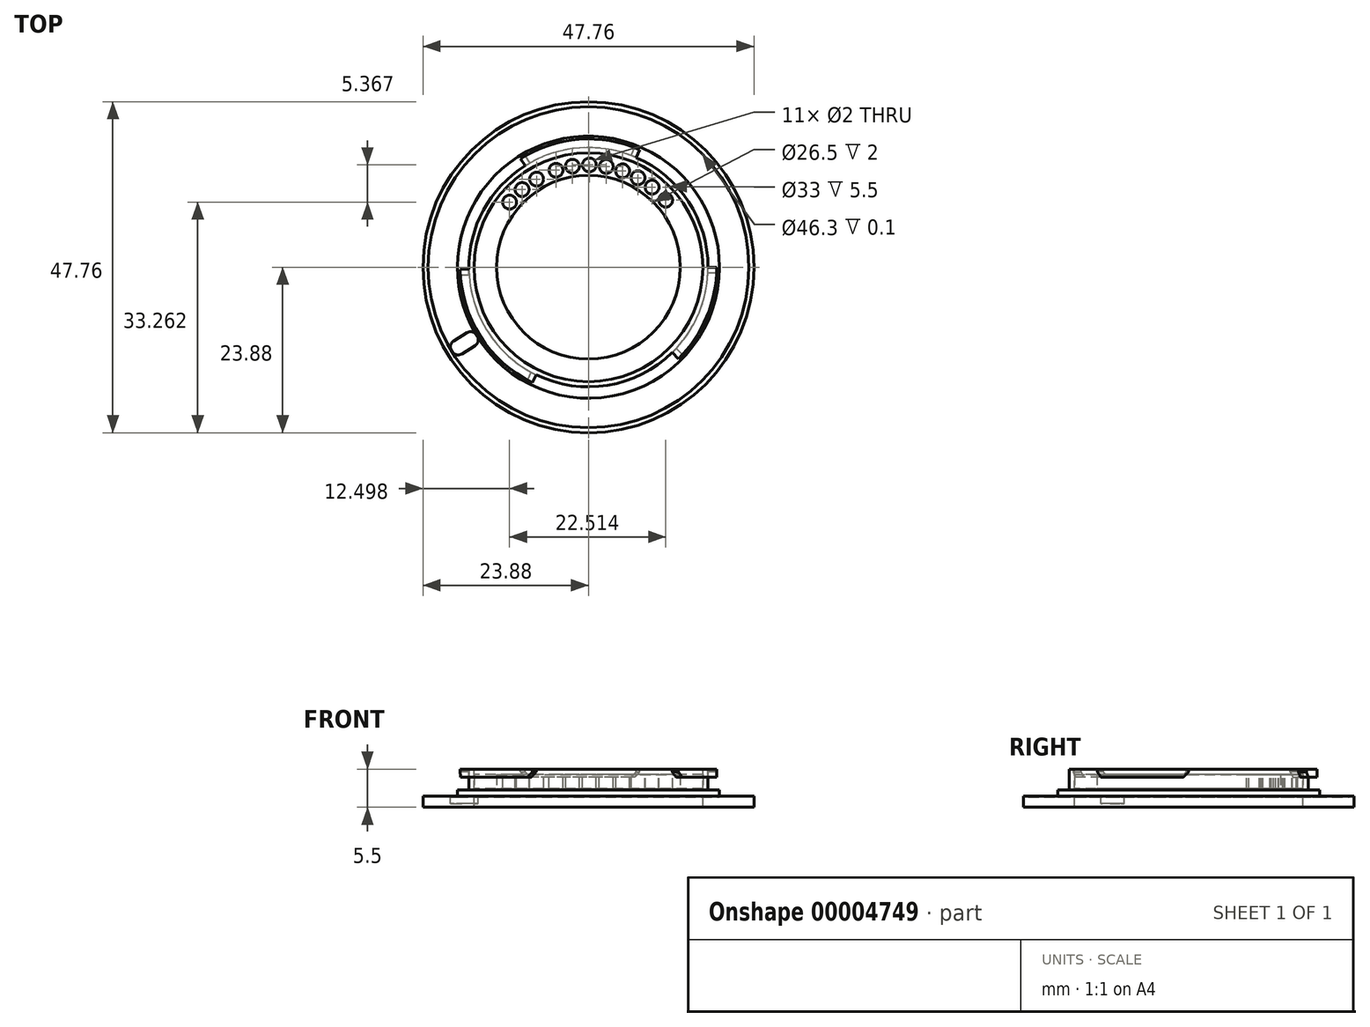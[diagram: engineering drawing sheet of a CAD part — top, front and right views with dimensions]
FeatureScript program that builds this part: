
annotation { "Feature Type Name" : "Feature", "Feature Type Description" : "" }
export const myFeature = defineFeature(function(context is Context, id is Id, definition is map)
    precondition{}
    {
        {
            var Q0;
            Q0=qCreatedBy(makeId("Top.planeOp"),FACE);
            var sketch = newSketch(context, id + "F0", { "sketchPlane" : qUnion([Q0])});
            skCircle(sketch, "E0", {"center": v(0, 0) * mm, "radius": 23.88 * mm});
            skCircle(sketch, "E1", {"center": v(0, 0) * mm, "radius": 23.15 * mm, "construction": true});
            skCircle(sketch, "E2", {"center": v(0, 0) * mm, "radius": 18.9 * mm, "construction": true});
            skCircle(sketch, "E3", {"center": v(0, 0) * mm, "radius": 16.5 * mm});
            skArc(sketch, "E4", {"start": v(-9.14, 14.63) * mm, "mid": v(-15.16, 8.23) * mm, "end": v(-17.25, -0.3) * mm, "construction": true});
            skArc(sketch, "E5", {"start": v(-18.5, -0.32) * mm, "mid": v(-15.6, -9.94) * mm, "end": v(-8.1, -16.63) * mm, "construction": true});
            skLineSegment(sketch, "E6", {"start": v(-19.74, -12.1) * mm, "end": v(0, 0) * mm, "construction": true});
            skLineSegment(sketch, "E7", {"start": v(-9.8, 15.69) * mm, "end": v(0, 0) * mm, "construction": true});
            skLineSegment(sketch, "E8", {"start": v(7.38, 16.97) * mm, "end": v(0, 0) * mm, "construction": true});
            skLineSegment(sketch, "E9", {"start": v(18.5, 0) * mm, "end": v(0, 0) * mm, "construction": true});
            skLineSegment(sketch, "E10", {"start": v(12.97, -13.2) * mm, "end": v(0, 0) * mm, "construction": true});
            skLineSegment(sketch, "E11", {"start": v(-8.1, -16.63) * mm, "end": v(0, 0) * mm, "construction": true});
            skLineSegment(sketch, "E12", {"start": v(-18.5, -0.32) * mm, "end": v(0, 0) * mm, "construction": true});
            skCircle(sketch, "E13", {"center": v(0, 0) * mm, "radius": 13.25 * mm, "construction": true});
            skLineSegment(sketch, "E14", {"start": v(-16.14, -9.77) * mm, "end": v(-16.04, -9.94) * mm});
            skLineSegment(sketch, "E15", {"start": v(-16.37, -11.32) * mm, "end": v(-18.29, -12.5) * mm, "construction": true});
            skLineSegment(sketch, "E16", {"start": v(-17.51, -9.44) * mm, "end": v(-19.44, -10.62) * mm, "construction": true});
            skLineSegment(sketch, "E17", {"start": v(-19.77, -12) * mm, "end": v(-19.66, -12.17) * mm});
            skLineSegment(sketch, "E18", {"start": v(-9.8, 15.69) * mm, "end": v(-9.14, 14.63) * mm});
            skLineSegment(sketch, "E19", {"start": v(7.38, 16.97) * mm, "end": v(6.88, 15.82) * mm});
            skLineSegment(sketch, "E20", {"start": v(17.25, 0) * mm, "end": v(18.5, 0) * mm});
            skLineSegment(sketch, "E21", {"start": v(12.1, -12.3) * mm, "end": v(12.97, -13.2) * mm});
            skLineSegment(sketch, "E22", {"start": v(-7.56, -15.5) * mm, "end": v(-8.1, -16.63) * mm});
            skLineSegment(sketch, "E23", {"start": v(-17.25, -0.3) * mm, "end": v(-18.5, -0.32) * mm});
            skArc(sketch, "E24.trimOffspring", {"start": v(17.25, 0) * mm, "mid": v(14.43, 9.46) * mm, "end": v(6.88, 15.82) * mm, "construction": true});
            skArc(sketch, "E25.trimOffspring", {"start": v(-7.56, -15.5) * mm, "mid": v(2.77, -17.03) * mm, "end": v(12.1, -12.3) * mm, "construction": true});
            skArc(sketch, "E26.trimOffspring", {"start": v(7.38, 16.97) * mm, "mid": v(-1.37, 18.45) * mm, "end": v(-9.8, 15.69) * mm, "construction": true});
            skArc(sketch, "E27.trimOffspring", {"start": v(12.97, -13.2) * mm, "mid": v(17.06, -7.15) * mm, "end": v(18.5, 0) * mm, "construction": true});
            skCircle(sketch, "E28", {"center": v(-11.38, 9.38) * mm, "radius": 1 * mm});
            skLineSegment(sketch, "E29", {"start": v(-11.38, 9.38) * mm, "end": v(0, 0) * mm, "construction": true});
            skCircle(sketch, "E30", {"center": v(-7.49, 12.7) * mm, "radius": 1 * mm});
            skLineSegment(sketch, "E31", {"start": v(-7.49, 12.7) * mm, "end": v(0, 0) * mm, "construction": true});
            skLineSegment(sketch, "E32", {"start": v(0, 0) * mm, "end": v(11.13, 9.68) * mm, "construction": true});
            skCircle(sketch, "E33", {"center": v(11.13, 9.68) * mm, "radius": 1 * mm});
            skLineSegment(sketch, "E34", {"start": v(9.18, 11.54) * mm, "end": v(0, 0) * mm, "construction": true});
            skLineSegment(sketch, "E35", {"start": v(7.15, 12.9) * mm, "end": v(0, 0) * mm, "construction": true});
            skLineSegment(sketch, "E36", {"start": v(4.92, 13.9) * mm, "end": v(0, 0) * mm, "construction": true});
            skLineSegment(sketch, "E37", {"start": v(2.56, 14.53) * mm, "end": v(0, 0) * mm, "construction": true});
            skLineSegment(sketch, "E38", {"start": v(0.13, 14.75) * mm, "end": v(0, 0) * mm, "construction": true});
            skLineSegment(sketch, "E39", {"start": v(-2.3, 14.57) * mm, "end": v(0, 0) * mm, "construction": true});
            skLineSegment(sketch, "E40", {"start": v(-4.68, 13.99) * mm, "end": v(0, 0) * mm, "construction": true});
            skLineSegment(sketch, "E41", {"start": v(-9.58, 11.22) * mm, "end": v(0, 0) * mm, "construction": true});
            skCircle(sketch, "E42", {"center": v(-9.58, 11.22) * mm, "radius": 1 * mm});
            skCircle(sketch, "E43", {"center": v(-4.68, 13.99) * mm, "radius": 1 * mm});
            skCircle(sketch, "E44", {"center": v(-2.3, 14.57) * mm, "radius": 1 * mm});
            skCircle(sketch, "E45", {"center": v(0.13, 14.75) * mm, "radius": 1 * mm});
            skCircle(sketch, "E46", {"center": v(2.56, 14.53) * mm, "radius": 1 * mm});
            skCircle(sketch, "E47", {"center": v(4.92, 13.9) * mm, "radius": 1 * mm});
            skCircle(sketch, "E48", {"center": v(7.15, 12.9) * mm, "radius": 1 * mm});
            skCircle(sketch, "E49", {"center": v(9.18, 11.54) * mm, "radius": 1 * mm});
            skPoint(sketch, "E50.visualSharp", {"position": v(-20.3, -11.14) * mm});
            skArc(sketch, "E50.filletArc", {"start": v(-19.44, -10.62) * mm, "mid": v(-19.89, -11.24) * mm, "end": v(-19.77, -12) * mm, "construction": true});
            skPoint(sketch, "E51.visualSharp", {"position": v(-19.14, -13.02) * mm});
            skLineSegment(sketch, "E52", {"start": v(-19.66, -12.17) * mm, "end": v(-19.66, -12.17) * mm});
            skArc(sketch, "E53.filletArc", {"start": v(-19.66, -12.17) * mm, "mid": v(-19.04, -12.62) * mm, "end": v(-18.29, -12.5) * mm, "construction": true});
            skPoint(sketch, "E54.visualSharp", {"position": v(-16.66, -8.92) * mm});
            skArc(sketch, "E54.filletArc", {"start": v(-16.14, -9.77) * mm, "mid": v(-16.76, -9.32) * mm, "end": v(-17.51, -9.44) * mm, "construction": true});
            skPoint(sketch, "E55.visualSharp", {"position": v(-15.51, -10.8) * mm});
            skArc(sketch, "E55.filletArc", {"start": v(-16.37, -11.32) * mm, "mid": v(-15.92, -10.7) * mm, "end": v(-16.04, -9.94) * mm, "construction": true});
            skSolve(sketch);
        }
        {
            var Q0;
            Q0=makeQuery(id+"F0.imprint","IMPRINT",FACE,{"disambiguationData":[TD([[makeQuery(id+"F0.imprint","IMPRINT",EDGE,{"derivedFrom":sQuery(id+"F0.wireOp",EDGE,"E0")}),1.0]])]});
            extrude(context, id + "F1", {"entities" : qUnion([Q0]), "oppositeDirection" : true, "depth" : 1.5 * mm});
        }
        {
            var Q0;
            Q0=makeQuery(id+"F0.imprint","IMPRINT",FACE,{"disambiguationData":[TD([[makeQuery(id+"F0.imprint","IMPRINT",EDGE,{"derivedFrom":sQuery(id+"F0.wireOp",EDGE,"E0")}),1.0]])]});
            var sketch = newSketch(context, id + "F2", { "sketchPlane" : qUnion([Q0])});
            skCircle(sketch, "E56.0", {"center": v(0, 0) * mm, "radius": 23.88 * mm});
            skCircle(sketch, "E57.0", {"center": v(0, 0) * mm, "radius": 23.15 * mm});
            skSolve(sketch);
        }
        {
            var Q0;
            Q0=makeQuery(id+"F2.imprint","IMPRINT",FACE,{"disambiguationData":[TD([[makeQuery(id+"F2.imprint","IMPRINT",EDGE,{"derivedFrom":sQuery(id+"F2.wireOp",EDGE,"E56.0")}),1.0]])]});
            extrude(context, id + "F3", {"entities" : qUnion([Q0]), "operationType" : NewBodyOperationType.ADD, "depth" : 0.1 * mm});
        }
        {
            var Q0;
            Q0=makeQuery(id+"F0.imprint","IMPRINT",FACE,{"disambiguationData":[TD([[makeQuery(id+"F0.imprint","IMPRINT",EDGE,{"derivedFrom":sQuery(id+"F0.wireOp",EDGE,"E0")}),1.0]])]});
            var sketch = newSketch(context, id + "F4", { "sketchPlane" : qUnion([Q0])});
            skCircle(sketch, "E58.0", {"center": v(0, 0) * mm, "radius": 18.9 * mm});
            skCircle(sketch, "E59.0", {"center": v(0, 0) * mm, "radius": 16.5 * mm});
            skSolve(sketch);
        }
        {
            var Q0;
            Q0=makeQuery(id+"F4.imprint","IMPRINT",FACE,{"disambiguationData":[TD([[makeQuery(id+"F4.imprint","IMPRINT",EDGE,{"derivedFrom":sQuery(id+"F4.wireOp",EDGE,"E58.0")}),1.0]])]});
            extrude(context, id + "F5", {"entities" : qUnion([Q0]), "operationType" : NewBodyOperationType.ADD, "depth" : 1 * mm});
        }
        {
            var Q0;
            Q0=makeQuery(id+"F5.opExtrude","CAP_FACE",FACE,{"disambiguationData":[OSD([sQuery(id+"F4.wireOp",EDGE,"E58.0"),sQuery(id+"F4.wireOp",EDGE,"E59.0")])],"isStart":false});
            var sketch = newSketch(context, id + "F6", { "sketchPlane" : qUnion([Q0])});
            skCircle(sketch, "E60.0", {"center": v(0, 0) * mm, "radius": 16.5 * mm});
            skCircle(sketch, "E61.converted", {"center": v(0, 0) * mm, "radius": 17.25 * mm});
            skPoint(sketch, "E62.orphan", {"position": v(-17.25, -0.3) * mm});
            skSolve(sketch);
        }
        {
            var Q0;
            Q0=makeQuery(id+"F6.imprint","IMPRINT",FACE,{"disambiguationData":[TD([[makeQuery(id+"F6.imprint","IMPRINT",EDGE,{"derivedFrom":sQuery(id+"F6.wireOp",EDGE,"E60.0")}),-1.0]])]});
            extrude(context, id + "F7", {"entities" : qUnion([Q0]), "operationType" : NewBodyOperationType.ADD, "depth" : 3 * mm});
        }
        {
            var Q0;
            Q0=makeQuery(id+"F7.opExtrude","CAP_FACE",FACE,{"disambiguationData":[OSD([sQuery(id+"F6.wireOp",EDGE,"E60.0"),sQuery(id+"F6.wireOp",EDGE,"E61.converted")])],"isStart":false});
            var sketch = newSketch(context, id + "F8", { "sketchPlane" : qUnion([Q0])});
            skCircle(sketch, "E63.0", {"center": v(0, 0) * mm, "radius": 16.5 * mm});
            skLineSegment(sketch, "E64.0", {"start": v(-17.25, -0.3) * mm, "end": v(-18.5, -0.32) * mm});
            skArc(sketch, "E65.0", {"start": v(-18.5, -0.32) * mm, "mid": v(-15.6, -9.94) * mm, "end": v(-8.1, -16.63) * mm});
            skLineSegment(sketch, "E66.0", {"start": v(-7.56, -15.5) * mm, "end": v(-8.1, -16.63) * mm});
            skArc(sketch, "E67.0", {"start": v(-7.56, -15.5) * mm, "mid": v(2.77, -17.03) * mm, "end": v(12.1, -12.3) * mm});
            skLineSegment(sketch, "E68.0", {"start": v(12.1, -12.3) * mm, "end": v(12.97, -13.2) * mm});
            skArc(sketch, "E69.0", {"start": v(12.97, -13.2) * mm, "mid": v(17.06, -7.15) * mm, "end": v(18.5, 0) * mm});
            skLineSegment(sketch, "E70.0", {"start": v(17.25, 0) * mm, "end": v(18.5, 0) * mm});
            skArc(sketch, "E71.0", {"start": v(17.25, 0) * mm, "mid": v(14.43, 9.46) * mm, "end": v(6.88, 15.82) * mm});
            skLineSegment(sketch, "E72.0", {"start": v(7.38, 16.97) * mm, "end": v(6.88, 15.82) * mm});
            skArc(sketch, "E73.0", {"start": v(7.38, 16.97) * mm, "mid": v(-1.37, 18.45) * mm, "end": v(-9.8, 15.69) * mm});
            skLineSegment(sketch, "E74.0", {"start": v(-9.8, 15.69) * mm, "end": v(-9.14, 14.63) * mm});
            skArc(sketch, "E75.0", {"start": v(-9.14, 14.63) * mm, "mid": v(-15.16, 8.23) * mm, "end": v(-17.25, -0.3) * mm});
            skSolve(sketch);
        }
        {
            var Q0;
            {var subQ3=sQuery(id+"F8.wireOp",EDGE,"E64.0");var subQ8=sQuery(id+"F8.wireOp",EDGE,"E68.0");var subQ11=sQuery(id+"F8.wireOp",EDGE,"E72.0");Q0=qUnion([makeQuery(id+"F8.imprint","IMPRINT",FACE,{"disambiguationData":[TD([[makeQuery(id+"F8.imprint","IMPRINT",EDGE,{"derivedFrom":subQ3}),1.0]])]}),makeQuery(id+"F8.imprint","IMPRINT",FACE,{"disambiguationData":[TD([[makeQuery(id+"F8.imprint","IMPRINT",EDGE,{"derivedFrom":subQ8}),1.0]])]}),makeQuery(id+"F8.imprint","IMPRINT",FACE,{"disambiguationData":[TD([[makeQuery(id+"F8.imprint","IMPRINT",EDGE,{"derivedFrom":subQ11}),-1.0]])]}),makeQuery(id+"F8.imprint","IMPRINT",FACE,{"disambiguationData":[TD([[makeQuery(id+"F8.imprint","IMPRINT",EDGE,{"derivedFrom":sQuery(id+"F8.wireOp",EDGE,"E63.0")}),-1.0]])]})]);}
            extrude(context, id + "F9", {"entities" : qUnion([Q0]), "operationType" : NewBodyOperationType.ADD, "oppositeDirection" : true, "depth" : 1.2 * mm});
        }
        {
            var Q0;
            Q0=makeQuery(id+"F1.opExtrude","CAP_FACE",FACE,{"disambiguationData":[OSD([sQuery(id+"F0.wireOp",EDGE,"E0"),sQuery(id+"F0.wireOp",EDGE,"E3")])],"isStart":true});
            var sketch = newSketch(context, id + "F10", { "sketchPlane" : qUnion([Q0])});
            skArc(sketch, "E76.0", {"start": v(-19.66, -12.17) * mm, "mid": v(-19.04, -12.62) * mm, "end": v(-18.29, -12.5) * mm});
            skLineSegment(sketch, "E77.0", {"start": v(-16.37, -11.32) * mm, "end": v(-18.29, -12.5) * mm});
            skArc(sketch, "E78.0", {"start": v(-16.37, -11.32) * mm, "mid": v(-15.92, -10.7) * mm, "end": v(-16.04, -9.94) * mm});
            skArc(sketch, "E79.0", {"start": v(-19.44, -10.62) * mm, "mid": v(-19.89, -11.24) * mm, "end": v(-19.77, -12) * mm});
            skLineSegment(sketch, "E80.0", {"start": v(-17.51, -9.44) * mm, "end": v(-19.44, -10.62) * mm});
            skArc(sketch, "E81.0", {"start": v(-16.14, -9.77) * mm, "mid": v(-16.76, -9.32) * mm, "end": v(-17.51, -9.44) * mm});
            skLineSegment(sketch, "E82.0", {"start": v(-16.14, -9.77) * mm, "end": v(-16.04, -9.94) * mm});
            skLineSegment(sketch, "E83.0", {"start": v(-19.77, -12) * mm, "end": v(-19.66, -12.17) * mm});
            skSolve(sketch);
        }
        {
            var Q0;
            {var subQ8=sQuery(id+"F10.wireOp",EDGE,"E82.0");Q0=qUnion([makeQuery(id+"F10.imprint","IMPRINT",FACE,{"disambiguationData":[TD([[makeQuery(id+"F10.imprint","IMPRINT",EDGE,{"derivedFrom":sQuery(id+"F10.wireOp",EDGE,"E76.0")}),1.0]])]}),makeQuery(id+"F10.imprint","IMPRINT",FACE,{"disambiguationData":[TD([[makeQuery(id+"F10.imprint","IMPRINT",EDGE,{"derivedFrom":subQ8}),-1.0]])]})]);}
            extrude(context, id + "F11", {"entities" : qUnion([Q0]), "operationType" : NewBodyOperationType.REMOVE, "oppositeDirection" : true, "depth" : 1 * mm});
        }
        {
            var Q0;
            Q0=makeQuery(id+"F9.opExtrude","CAP_EDGE",EDGE,{"disambiguationData":[OSD([sQuery(id+"F8.wireOp",EDGE,"E72.0")])],"isStart":false});
            var Q1;
            Q1=makeQuery(id+"F9.opExtrude","CAP_EDGE",EDGE,{"disambiguationData":[OSD([sQuery(id+"F8.wireOp",EDGE,"E74.0")])],"isStart":false});
            var Q2;
            Q2=makeQuery(id+"F9.opExtrude","CAP_EDGE",EDGE,{"disambiguationData":[OSD([sQuery(id+"F8.wireOp",EDGE,"E70.0")])],"isStart":false});
            var Q3;
            Q3=makeQuery(id+"F9.opExtrude","CAP_EDGE",EDGE,{"disambiguationData":[OSD([sQuery(id+"F8.wireOp",EDGE,"E68.0")])],"isStart":false});
            var Q4;
            Q4=makeQuery(id+"F9.opExtrude","CAP_EDGE",EDGE,{"disambiguationData":[OSD([sQuery(id+"F8.wireOp",EDGE,"E66.0")])],"isStart":false});
            var Q5;
            Q5=makeQuery(id+"F9.opExtrude","CAP_EDGE",EDGE,{"disambiguationData":[OSD([sQuery(id+"F8.wireOp",EDGE,"E64.0")])],"isStart":false});
            chamfer(context, id + "F12", {"entities" : qUnion([Q0, Q1, Q2, Q3, Q4, Q5]), "width" : 0.8 * mm, "tangentPropagation" : true});
        }
        {
            var Q0;
            Q0=makeQuery(id+"F1.opExtrude","CAP_FACE",FACE,{"disambiguationData":[OSD([sQuery(id+"F0.wireOp",EDGE,"E0"),sQuery(id+"F0.wireOp",EDGE,"E3")])],"isStart":false});
            var sketch = newSketch(context, id + "F13", { "sketchPlane" : qUnion([Q0])});
            skCircle(sketch, "E84.0", {"center": v(0, 0) * mm, "radius": 16.5 * mm});
            skCircle(sketch, "E85.0", {"center": v(0, 0) * mm, "radius": 13.25 * mm});
            skSolve(sketch);
        }
        {
            var Q0;
            Q0=makeQuery(id+"F13.imprint","IMPRINT",FACE,{"disambiguationData":[TD([[makeQuery(id+"F13.imprint","IMPRINT",EDGE,{"derivedFrom":sQuery(id+"F13.wireOp",EDGE,"E84.0")}),-1.0]])]});
            extrude(context, id + "F14", {"entities" : qUnion([Q0]), "oppositeDirection" : true, "depth" : 2 * mm});
        }
        {
            var Q0;
            Q0=makeQuery(id+"F14.opExtrude","SWEPT_BODY",BODY,{"disambiguationData":[OSD([sQuery(id+"F13.wireOp",EDGE,"E84.0"),sQuery(id+"F13.wireOp",EDGE,"E85.0")])]});
            var Q1;
            Q1=makeQuery(id+"F9.boolean.opBoolean","MERGE",FACE,{"derivedFrom":[makeQuery(id+"F7.opExtrude","CAP_FACE",FACE,{"disambiguationData":[OSD([sQuery(id+"F6.wireOp",EDGE,"E60.0"),sQuery(id+"F6.wireOp",EDGE,"E61.converted")])],"isStart":false}),makeQuery(id+"F9.opExtrude","CAP_FACE",FACE,{"disambiguationData":[OSD([sQuery(id+"F8.wireOp",EDGE,"E63.0"),sQuery(id+"F8.wireOp",EDGE,"E64.0"),sQuery(id+"F8.wireOp",EDGE,"E65.0"),sQuery(id+"F8.wireOp",EDGE,"E66.0"),sQuery(id+"F8.wireOp",EDGE,"E67.0"),sQuery(id+"F8.wireOp",EDGE,"E68.0"),sQuery(id+"F8.wireOp",EDGE,"E69.0"),sQuery(id+"F8.wireOp",EDGE,"E70.0"),sQuery(id+"F8.wireOp",EDGE,"E71.0"),sQuery(id+"F8.wireOp",EDGE,"E72.0"),sQuery(id+"F8.wireOp",EDGE,"E73.0"),sQuery(id+"F8.wireOp",EDGE,"E74.0"),sQuery(id+"F8.wireOp",EDGE,"E75.0")])],"isStart":true})]});
            transform(context, id + "F15", {"entities" : qUnion([Q0]), "transformType" : TransformType.TRANSLATION_DISTANCE, "transformDirection" : qUnion([Q1]), "distance" : 2.7 * mm, "makeCopy" : false});
        }
        {
            var Q0;
            Q0=makeQuery(id+"F14.opExtrude","CAP_FACE",FACE,{"disambiguationData":[OSD([sQuery(id+"F13.wireOp",EDGE,"E84.0"),sQuery(id+"F13.wireOp",EDGE,"E85.0")])],"isStart":false});
            var sketch = newSketch(context, id + "F16", { "sketchPlane" : qUnion([Q0])});
            skCircle(sketch, "E86.0", {"center": v(-11.38, 9.38) * mm, "radius": 1 * mm});
            skCircle(sketch, "E87.0", {"center": v(-9.58, 11.22) * mm, "radius": 1 * mm});
            skCircle(sketch, "E88.0", {"center": v(-7.49, 12.7) * mm, "radius": 1 * mm});
            skCircle(sketch, "E89.0", {"center": v(-4.68, 13.99) * mm, "radius": 1 * mm});
            skCircle(sketch, "E90.0", {"center": v(-2.3, 14.57) * mm, "radius": 1 * mm});
            skCircle(sketch, "E91.0", {"center": v(0.13, 14.75) * mm, "radius": 1 * mm});
            skCircle(sketch, "E92.0", {"center": v(2.56, 14.53) * mm, "radius": 1 * mm});
            skCircle(sketch, "E93.0", {"center": v(4.92, 13.9) * mm, "radius": 1 * mm});
            skCircle(sketch, "E94.0", {"center": v(7.15, 12.9) * mm, "radius": 1 * mm});
            skCircle(sketch, "E95.0", {"center": v(9.18, 11.54) * mm, "radius": 1 * mm});
            skCircle(sketch, "E96.0", {"center": v(11.13, 9.68) * mm, "radius": 1 * mm});
            skSolve(sketch);
        }
        {
            var Q0;
            Q0=makeQuery(id+"F16.imprint","IMPRINT",FACE,{"disambiguationData":[TD([[makeQuery(id+"F16.imprint","IMPRINT",EDGE,{"derivedFrom":sQuery(id+"F16.wireOp",EDGE,"E86.0")}),1.0]])]});
            var Q1;
            Q1=makeQuery(id+"F16.imprint","IMPRINT",FACE,{"disambiguationData":[TD([[makeQuery(id+"F16.imprint","IMPRINT",EDGE,{"derivedFrom":sQuery(id+"F16.wireOp",EDGE,"E87.0")}),1.0]])]});
            var Q2;
            Q2=makeQuery(id+"F16.imprint","IMPRINT",FACE,{"disambiguationData":[TD([[makeQuery(id+"F16.imprint","IMPRINT",EDGE,{"derivedFrom":sQuery(id+"F16.wireOp",EDGE,"E88.0")}),1.0]])]});
            var Q3;
            Q3=makeQuery(id+"F16.imprint","IMPRINT",FACE,{"disambiguationData":[TD([[makeQuery(id+"F16.imprint","IMPRINT",EDGE,{"derivedFrom":sQuery(id+"F16.wireOp",EDGE,"E89.0")}),1.0]])]});
            var Q4;
            Q4=makeQuery(id+"F16.imprint","IMPRINT",FACE,{"disambiguationData":[TD([[makeQuery(id+"F16.imprint","IMPRINT",EDGE,{"derivedFrom":sQuery(id+"F16.wireOp",EDGE,"E90.0")}),1.0]])]});
            var Q5;
            Q5=makeQuery(id+"F16.imprint","IMPRINT",FACE,{"disambiguationData":[TD([[makeQuery(id+"F16.imprint","IMPRINT",EDGE,{"derivedFrom":sQuery(id+"F16.wireOp",EDGE,"E91.0")}),1.0]])]});
            var Q6;
            Q6=makeQuery(id+"F16.imprint","IMPRINT",FACE,{"disambiguationData":[TD([[makeQuery(id+"F16.imprint","IMPRINT",EDGE,{"derivedFrom":sQuery(id+"F16.wireOp",EDGE,"E92.0")}),1.0]])]});
            var Q7;
            Q7=makeQuery(id+"F16.imprint","IMPRINT",FACE,{"disambiguationData":[TD([[makeQuery(id+"F16.imprint","IMPRINT",EDGE,{"derivedFrom":sQuery(id+"F16.wireOp",EDGE,"E93.0")}),1.0]])]});
            var Q8;
            Q8=makeQuery(id+"F16.imprint","IMPRINT",FACE,{"disambiguationData":[TD([[makeQuery(id+"F16.imprint","IMPRINT",EDGE,{"derivedFrom":sQuery(id+"F16.wireOp",EDGE,"E94.0")}),1.0]])]});
            var Q9;
            Q9=makeQuery(id+"F16.imprint","IMPRINT",FACE,{"disambiguationData":[TD([[makeQuery(id+"F16.imprint","IMPRINT",EDGE,{"derivedFrom":sQuery(id+"F16.wireOp",EDGE,"E95.0")}),1.0]])]});
            var Q10;
            Q10=makeQuery(id+"F16.imprint","IMPRINT",FACE,{"disambiguationData":[TD([[makeQuery(id+"F16.imprint","IMPRINT",EDGE,{"derivedFrom":sQuery(id+"F16.wireOp",EDGE,"E96.0")}),1.0]])]});
            extrude(context, id + "F17", {"entities" : qUnion([Q0, Q1, Q2, Q3, Q4, Q5, Q6, Q7, Q8, Q9, Q10]), "operationType" : NewBodyOperationType.REMOVE, "endBound" : BoundingType.THROUGH_ALL, "oppositeDirection" : true, "depth" : 25 * mm});
        }
    });
